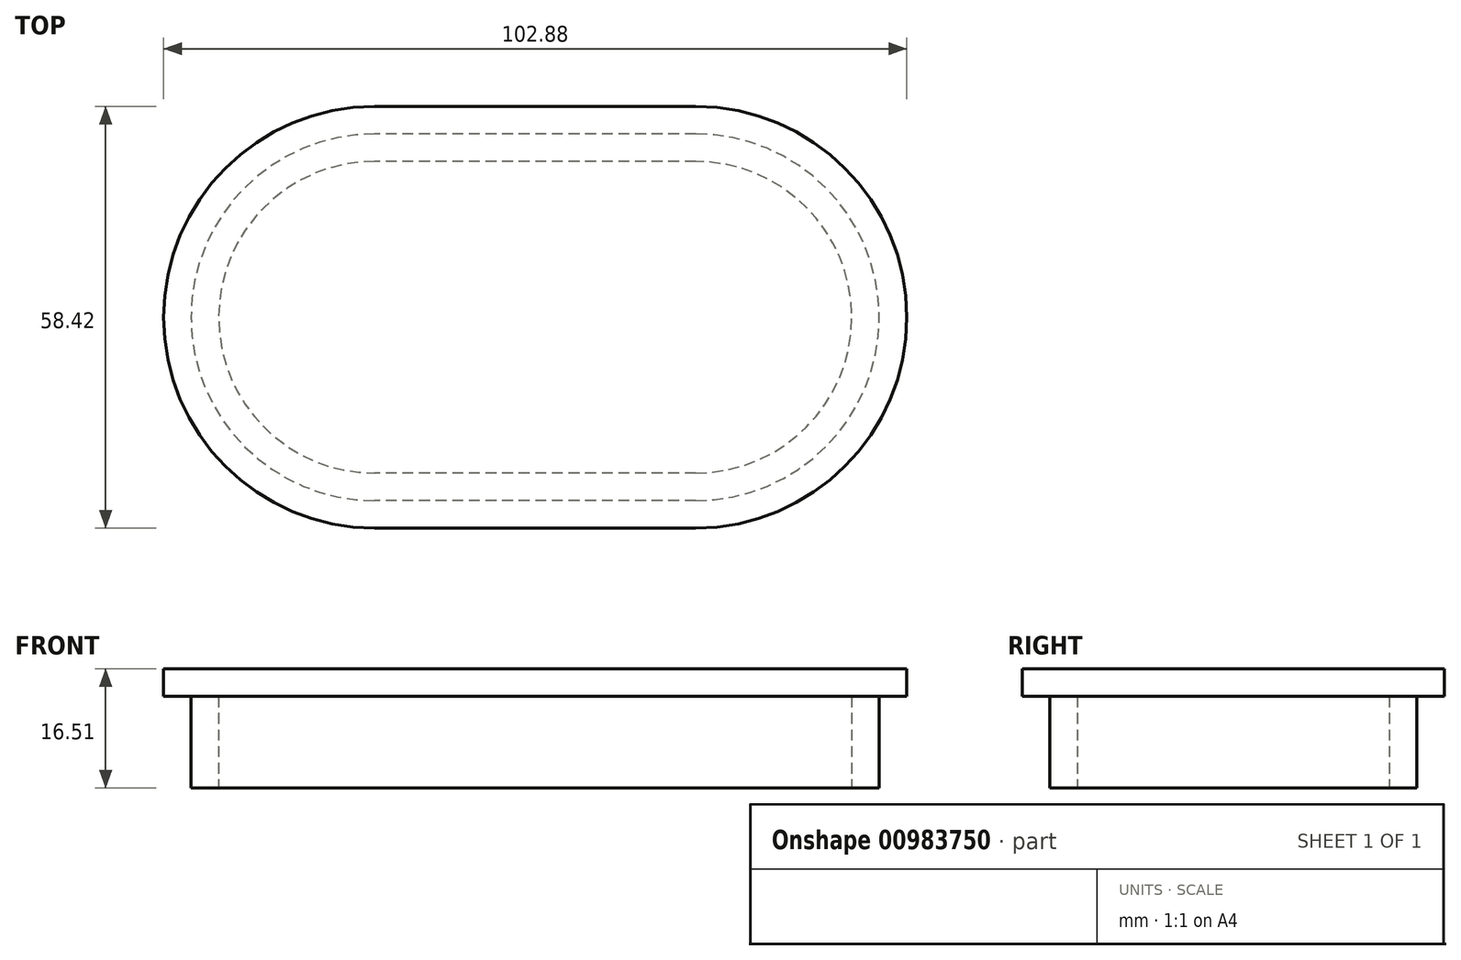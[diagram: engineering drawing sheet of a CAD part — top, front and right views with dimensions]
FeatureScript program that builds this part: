
annotation { "Feature Type Name" : "Feature", "Feature Type Description" : "" }
export const myFeature = defineFeature(function(context is Context, id is Id, definition is map)
    precondition{}
    {
        {
            var Q0;
            Q0=qCreatedBy(makeId("Top.planeOp"),FACE);
            var sketch = newSketch(context, id + "F0", { "sketchPlane" : qUnion([Q0])});
            skLineSegment(sketch, "E0.bottom", {"start": v(22.23, 21.6) * mm, "end": v(-22.23, 21.6) * mm});
            skLineSegment(sketch, "E0.top", {"start": v(22.23, -21.59) * mm, "end": v(-22.23, -21.59) * mm});
            skLineSegment(sketch, "E0.left", {"start": v(22.23, 21.59) * mm, "end": v(22.23, -21.59) * mm, "construction": true});
            skLineSegment(sketch, "E0.right", {"start": v(-22.23, 21.6) * mm, "end": v(-22.23, -21.6) * mm, "construction": true});
            skPoint(sketch, "E0.middle", {"position": v(0, 0) * mm});
            skArc(sketch, "E1", {"start": v(-22.23, 21.59) * mm, "mid": v(-43.82, 0) * mm, "end": v(-22.23, -21.59) * mm});
            skArc(sketch, "E2", {"start": v(22.23, 21.6) * mm, "mid": v(43.82, 0) * mm, "end": v(22.23, -21.59) * mm});
            skLineSegment(sketch, "E3.0", {"start": v(22.23, 25.4) * mm, "end": v(-22.23, 25.4) * mm});
            skArc(sketch, "E3.1", {"start": v(22.23, 25.4) * mm, "mid": v(47.63, 0) * mm, "end": v(22.23, -25.4) * mm});
            skLineSegment(sketch, "E3.2", {"start": v(22.23, -25.4) * mm, "end": v(-22.23, -25.4) * mm});
            skArc(sketch, "E3.3", {"start": v(-22.23, 25.4) * mm, "mid": v(-47.62, 0) * mm, "end": v(-22.23, -25.4) * mm});
            skSolve(sketch);
        }
        {
            var Q0;
            Q0 = qSketchRegion(id + "F0", true);
            extrude(context, id + "F1", {"entities" : qUnion([Q0]), "depth" : 12.7 * mm, "offsetDistance" : 25.4 * mm});
        }
        {
            var Q0;
            Q0=makeQuery(id+"F1.opExtrude","CAP_FACE",FACE,{"disambiguationData":[OSD([sQuery(id+"F0.wireOp",EDGE,"E0.bottom"),sQuery(id+"F0.wireOp",EDGE,"E0.top"),sQuery(id+"F0.wireOp",EDGE,"E1"),sQuery(id+"F0.wireOp",EDGE,"E2"),sQuery(id+"F0.wireOp",EDGE,"E3.0"),sQuery(id+"F0.wireOp",EDGE,"E3.1"),sQuery(id+"F0.wireOp",EDGE,"E3.2"),sQuery(id+"F0.wireOp",EDGE,"E3.3")])],"isStart":false});
            var sketch = newSketch(context, id + "F2", { "sketchPlane" : qUnion([Q0])});
            skLineSegment(sketch, "E4.0", {"start": v(22.23, 29.21) * mm, "end": v(-22.23, 29.21) * mm});
            skArc(sketch, "E4.1", {"start": v(22.23, 29.21) * mm, "mid": v(51.44, 0) * mm, "end": v(22.23, -29.21) * mm});
            skLineSegment(sketch, "E4.2", {"start": v(22.23, -29.21) * mm, "end": v(-22.23, -29.21) * mm});
            skArc(sketch, "E4.3", {"start": v(-22.23, 29.21) * mm, "mid": v(-51.44, 0) * mm, "end": v(-22.23, -29.21) * mm});
            skSolve(sketch);
        }
        {
            var Q0;
            Q0 = qSketchRegion(id + "F2", true);
            extrude(context, id + "F3", {"entities" : qUnion([Q0]), "operationType" : NewBodyOperationType.ADD, "depth" : 3.8 * mm, "offsetDistance" : 25.4 * mm});
        }
    });
